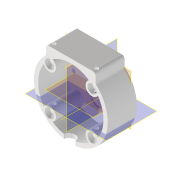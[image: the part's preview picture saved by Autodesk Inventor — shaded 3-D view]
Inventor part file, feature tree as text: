
AUTODESK INVENTOR PART (.ipt)
format: ipt  version: 2022.5 (Build 265521000, 521)  size: 323,072 bytes
history: native  units: mm
features: reference x12, sketch x7, plane x5, extrude x5, projected_geometry x3, other x3, hole x2, fillet x1
ambient origin geometry x8: Origin, YZ Plane, XZ Plane, XY Plane, X Axis, Y Axis, Z Axis, Center Point
bodies: Volumenkörper1 (feature_tree)
feature tree (38):
  plane  "Arbeitsebene1"
  extrude  "Extrusion1"  Depth=2.8mm
  sketch  "Skizze2"  dims[d2=2.8mm d3=12.0mm]
  plane  "Arbeitsebene2"
  extrude  "Extrusion2"  Depth=12.0mm
  plane  "Arbeitsebene4"
  extrude  "Extrusion4"  Depth=3.0mm
  extrude  "Extrusion5"  Depth=2.8mm
  fillet  "Rundung1"  [1 undecoded]
  hole  "Bohrung1"  [1 undecoded]
  hole  "Bohrung2"  [1 undecoded]
  plane  "Arbeitsebene5"
  extrude  "Extrusion6"  Depth=3.5mm
  sketch  "Skizze1"  dims[d0=52.0mm d1=2.8mm]
  reference  "Referenz1"
  reference  "Referenz2"
  reference  "Referenz3"
  reference  "Referenz4"
  projected_geometry  "Projizierte Kontur1"
  reference  "Referenz5"
  reference  "Referenz6"
  reference  "Referenz7"
  reference  "Referenz8"
  reference  "Referenz9"
  reference  "Referenz10"
  reference  "Referenz11"
  reference  "Referenz12"
  plane  "Arbeitsebene3"
  other  "Arbeitsachse1"
  sketch  "Skizze6"  dims[d4=1.0mm d5=0.0mm d6=3.0mm]
  sketch  "Skizze7"  dims[d7=3.0mm d8=0.0mm d9=2.8mm d15=90.0deg]
  projected_geometry  "Projizierte Kontur2"
  sketch  "Skizze8"  dims[d26=10.0mm d27=0.0mm d28=35.0mm]
  sketch  "Skizze9"  dims[d30=1.0mm d31=0.0mm d32=2.0mm]
  projected_geometry  "Projizierte Kontur3"
  sketch  "Skizze10"  dims[d33=30.0mm d34=35.0mm d35=2.8mm d36=6.0mm d37=4.0mm d38=2.0mm d39=90.0deg d40=8.0mm d41=20.594885mm d42=3.0mm d43=3.0mm d44=3.0mm d45=3.0mm d46=2.8mm d47=6.0mm d48=6.5mm d49=3.5mm d50=90.0deg d51=30.0mm d52=20.594885mm d53=-27.0mm d54=8.0mm d55=0.0mm d56=0.0mm]
  other  "Planktoscope_Mini_Peristalticpump_new.iam"
  other  "00_Stepper_Motor_28BYJ-48:1"
note: 3 required parameter values undecoded (feature->parameter linkage not recoverable at this tier; creation-order binding heuristic only, values carry confidence <= 0.55)
